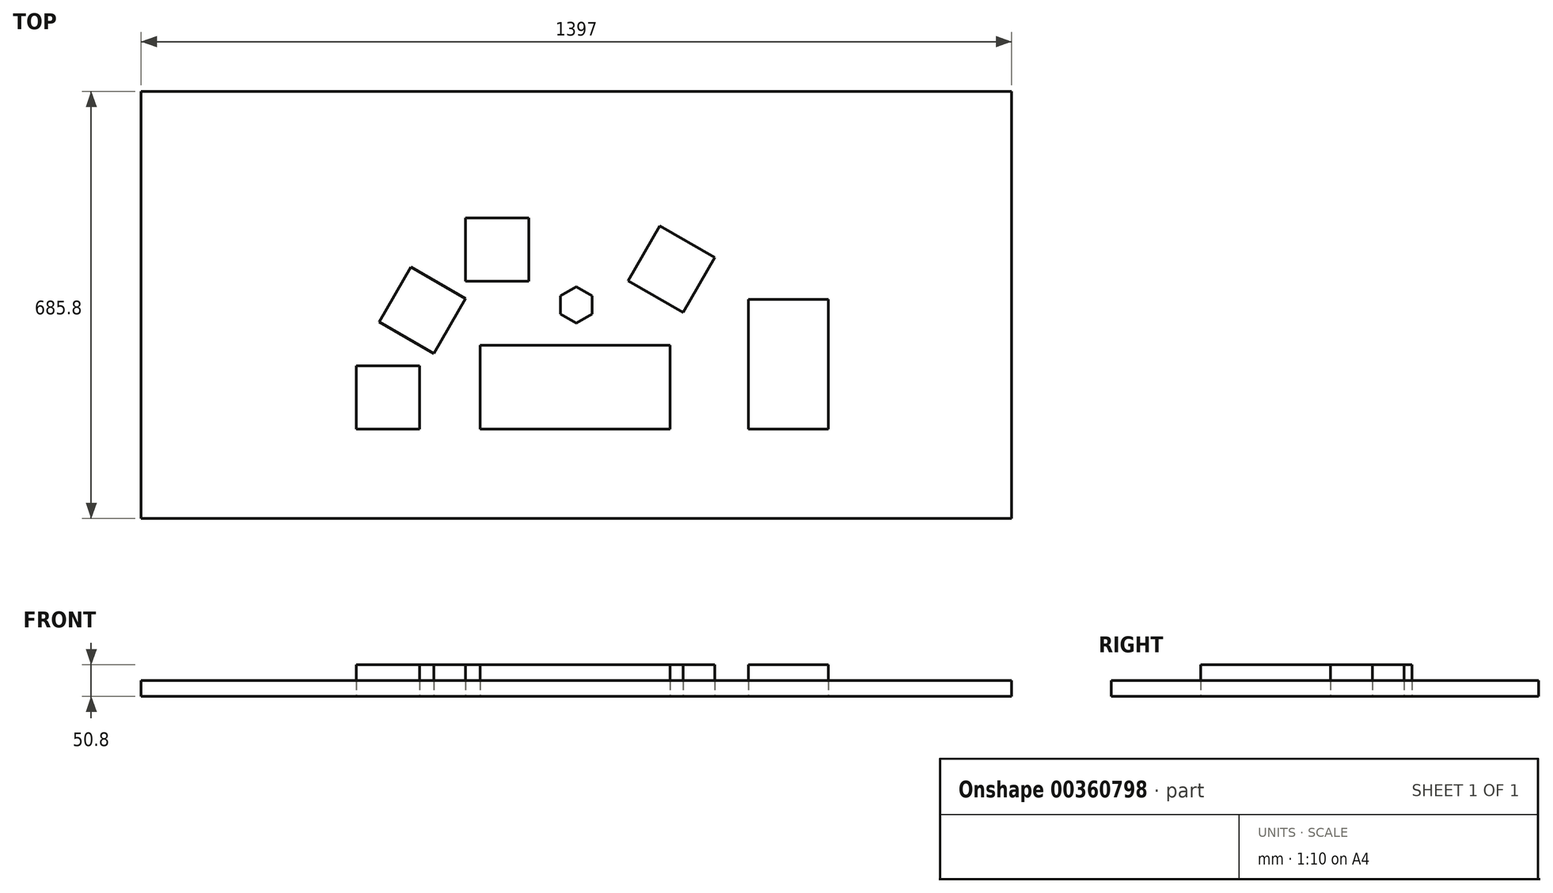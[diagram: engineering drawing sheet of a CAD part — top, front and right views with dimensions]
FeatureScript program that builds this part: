
annotation { "Feature Type Name" : "Feature", "Feature Type Description" : "" }
export const myFeature = defineFeature(function(context is Context, id is Id, definition is map)
    precondition{}
    {
        {
            var Q0;
            Q0=qCreatedBy(makeId("Top.planeOp"),FACE);
            var sketch = newSketch(context, id + "F0", { "sketchPlane" : qUnion([Q0])});
            skLineSegment(sketch, "E0.bottom", {"start": v(698.5, -342.9) * mm, "end": v(-698.5, -342.9) * mm});
            skLineSegment(sketch, "E0.top", {"start": v(698.5, 342.9) * mm, "end": v(-698.5, 342.9) * mm});
            skLineSegment(sketch, "E0.left", {"start": v(698.5, -342.9) * mm, "end": v(698.5, 342.9) * mm});
            skLineSegment(sketch, "E0.right", {"start": v(-698.5, -342.9) * mm, "end": v(-698.5, 342.9) * mm});
            skPoint(sketch, "E0.middle", {"position": v(0, 0) * mm});
            skSolve(sketch);
        }
        {
            var Q0;
            Q0 = qSketchRegion(id + "F0", true);
            extrude(context, id + "F1", {"entities" : qUnion([Q0]), "depth" : 25.4 * mm});
        }
        {
            var Q0;
            Q0=makeQuery(id+"F1.opExtrude","CAP_FACE",FACE,{"disambiguationData":[OSD([sQuery(id+"F0.wireOp",EDGE,"E0.bottom"),sQuery(id+"F0.wireOp",EDGE,"E0.top"),sQuery(id+"F0.wireOp",EDGE,"E0.left"),sQuery(id+"F0.wireOp",EDGE,"E0.right")])],"isStart":false});
            var sketch = newSketch(context, id + "F2", { "sketchPlane" : qUnion([Q0])});
            skLineSegment(sketch, "E1.bottom", {"start": v(-154.32, -64.63) * mm, "end": v(150.48, -64.63) * mm});
            skLineSegment(sketch, "E1.top", {"start": v(-154.32, -199.25) * mm, "end": v(150.48, -199.25) * mm});
            skLineSegment(sketch, "E1.left", {"start": v(-154.32, -64.63) * mm, "end": v(-154.32, -199.25) * mm});
            skLineSegment(sketch, "E1.right", {"start": v(150.48, -64.63) * mm, "end": v(150.48, -199.25) * mm});
            skLineSegment(sketch, "E2.bottom", {"start": v(-353.16, -97.65) * mm, "end": v(-251.56, -97.65) * mm});
            skLineSegment(sketch, "E2.top", {"start": v(-353.16, -199.25) * mm, "end": v(-251.56, -199.25) * mm});
            skLineSegment(sketch, "E2.left", {"start": v(-353.16, -97.65) * mm, "end": v(-353.16, -199.25) * mm});
            skLineSegment(sketch, "E2.right", {"start": v(-251.56, -97.65) * mm, "end": v(-251.56, -199.25) * mm});
            skCircle(sketch, "E3.cCircle", {"center": v(0, 0) * mm, "radius": 25.4 * mm, "construction": true});
            skLineSegment(sketch, "E3.0", {"start": v(25.4, 14.66) * mm, "end": v(25.4, -14.66) * mm});
            skLineSegment(sketch, "E3.1", {"start": v(25.4, -14.66) * mm, "end": v(0, -29.33) * mm});
            skLineSegment(sketch, "E3.2", {"start": v(0, -29.33) * mm, "end": v(-25.4, -14.66) * mm});
            skLineSegment(sketch, "E3.3", {"start": v(-25.4, -14.66) * mm, "end": v(-25.4, 14.66) * mm});
            skLineSegment(sketch, "E3.4", {"start": v(-25.4, 14.66) * mm, "end": v(0, 29.33) * mm});
            skLineSegment(sketch, "E3.5", {"start": v(0, 29.33) * mm, "end": v(25.4, 14.66) * mm});
            skPoint(sketch, "E3.0.midPoint", {"position": v(25.4, 0) * mm});
            skLineSegment(sketch, "E4", {"start": v(-1.92, -335.66) * mm, "end": v(-1.92, 257.78) * mm});
            skPoint(sketch, "E4.startSnap0", {"position": v(-1.92, -199.25) * mm});
            skLineSegment(sketch, "E5.bottom", {"start": v(276.1, 8.5) * mm, "end": v(404.48, 8.5) * mm});
            skLineSegment(sketch, "E5.top", {"start": v(276.1, -199.25) * mm, "end": v(404.48, -199.25) * mm});
            skLineSegment(sketch, "E5.left", {"start": v(276.1, 8.5) * mm, "end": v(276.1, -199.25) * mm});
            skLineSegment(sketch, "E5.right", {"start": v(404.48, 8.5) * mm, "end": v(404.48, -199.25) * mm});
            skLineSegment(sketch, "E6.bottom", {"start": v(-265.79, 60.6) * mm, "end": v(-177.8, 9.8) * mm});
            skLineSegment(sketch, "E6.top", {"start": v(-316.59, -27.4) * mm, "end": v(-228.6, -78.2) * mm});
            skLineSegment(sketch, "E6.left", {"start": v(-265.79, 60.6) * mm, "end": v(-316.59, -27.4) * mm});
            skLineSegment(sketch, "E6.right", {"start": v(-177.8, 9.8) * mm, "end": v(-228.6, -78.2) * mm});
            skLineSegment(sketch, "E7.bottom", {"start": v(-177.8, 139.63) * mm, "end": v(-76.2, 139.63) * mm});
            skLineSegment(sketch, "E7.top", {"start": v(-177.8, 38.03) * mm, "end": v(-76.2, 38.03) * mm});
            skLineSegment(sketch, "E7.left", {"start": v(-177.8, 139.63) * mm, "end": v(-177.8, 38.03) * mm});
            skLineSegment(sketch, "E7.right", {"start": v(-76.2, 139.63) * mm, "end": v(-76.2, 38.03) * mm});
            skLineSegment(sketch, "E8.bottom", {"start": v(133.8, 126.7) * mm, "end": v(221.8, 75.9) * mm});
            skLineSegment(sketch, "E8.top", {"start": v(83, 38.7) * mm, "end": v(171, -12.1) * mm});
            skLineSegment(sketch, "E8.left", {"start": v(133.8, 126.7) * mm, "end": v(83, 38.7) * mm});
            skLineSegment(sketch, "E8.right", {"start": v(221.8, 75.9) * mm, "end": v(171, -12.1) * mm});
            skPoint(sketch, "E9", {"position": v(-127, 38.03) * mm});
            skPoint(sketch, "E10", {"position": v(127, 13.3) * mm});
            skPoint(sketch, "E11", {"position": v(276.1, -95.38) * mm});
            skPoint(sketch, "E12", {"position": v(-203.2, -34.2) * mm});
            skPoint(sketch, "E13", {"position": v(-251.56, -148.45) * mm});
            skSolve(sketch);
        }
        {
            var Q0;
            Q0 = qSketchRegion(id + "F2", true);
            extrude(context, id + "F3", {"entities" : qUnion([Q0]), "depth" : 25.4 * mm, "hasSecondDirection" : true, "secondDirectionOppositeDirection" : true, "secondDirectionDepth" : 25.4 * mm});
        }
    });
